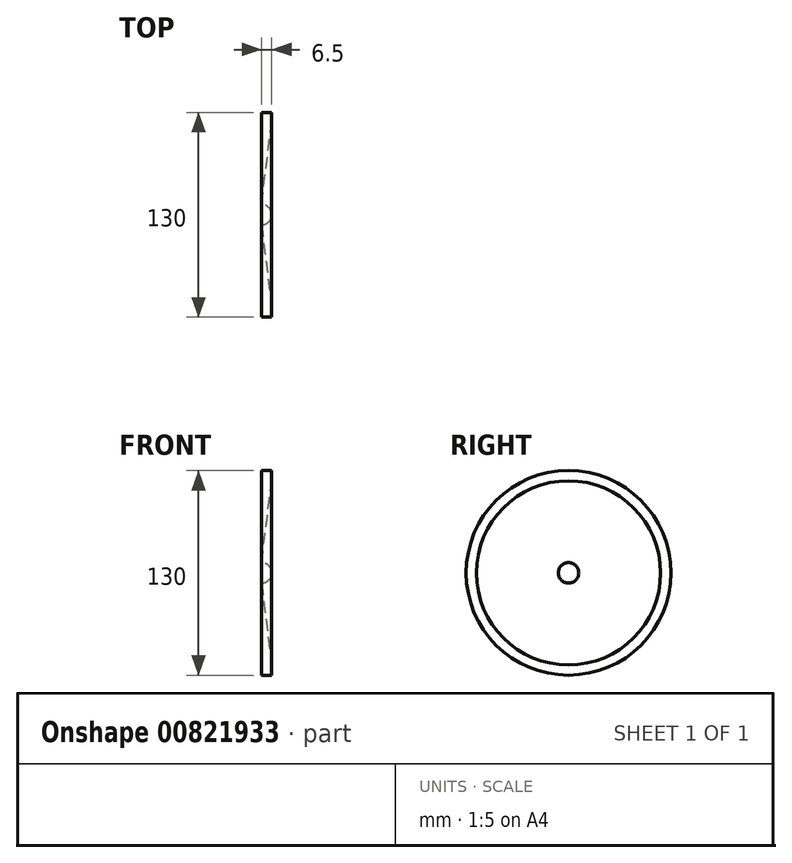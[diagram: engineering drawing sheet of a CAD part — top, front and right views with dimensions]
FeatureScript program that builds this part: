
annotation { "Feature Type Name" : "Feature", "Feature Type Description" : "" }
export const myFeature = defineFeature(function(context is Context, id is Id, definition is map)
    precondition{}
    {
        {
            var Q0;
            Q0=qCreatedBy(makeId("Front.planeOp"),FACE);
            var sketch = newSketch(context, id + "F0", { "sketchPlane" : qUnion([Q0])});
            skLineSegment(sketch, "E0", {"start": v(0, 0) * mm, "end": v(0, 65) * mm});
            skLineSegment(sketch, "E1", {"start": v(0, 65) * mm, "end": v(6.5, 65) * mm});
            skArc(sketch, "E2", {"start": v(0, 6.5) * mm, "mid": v(4.6, 4.6) * mm, "end": v(6.5, 0) * mm});
            skLineSegment(sketch, "E3", {"start": v(0, 0) * mm, "end": v(6.5, 0) * mm});
            skLineSegment(sketch, "E4", {"start": v(6.5, 65) * mm, "end": v(6.5, 58.5) * mm});
            skLineSegment(sketch, "E5", {"start": v(0, 6.5) * mm, "end": v(6.5, 58.5) * mm});
            skSolve(sketch);
        }
        {
            var Q0;
            Q0=qSketchRegion(id+"F0",true);
            var Q1;
            Q1=sQuery(id+"F0.wireOp",EDGE,"E3");
            revolve(context, id + "F1", {"surfaceOperationType" : NewSurfaceOperationType.NEW, "entities" : qUnion([Q0]), "axis" : qUnion([Q1]), "revolveType" : RevolveType.FULL});
        }
    });
